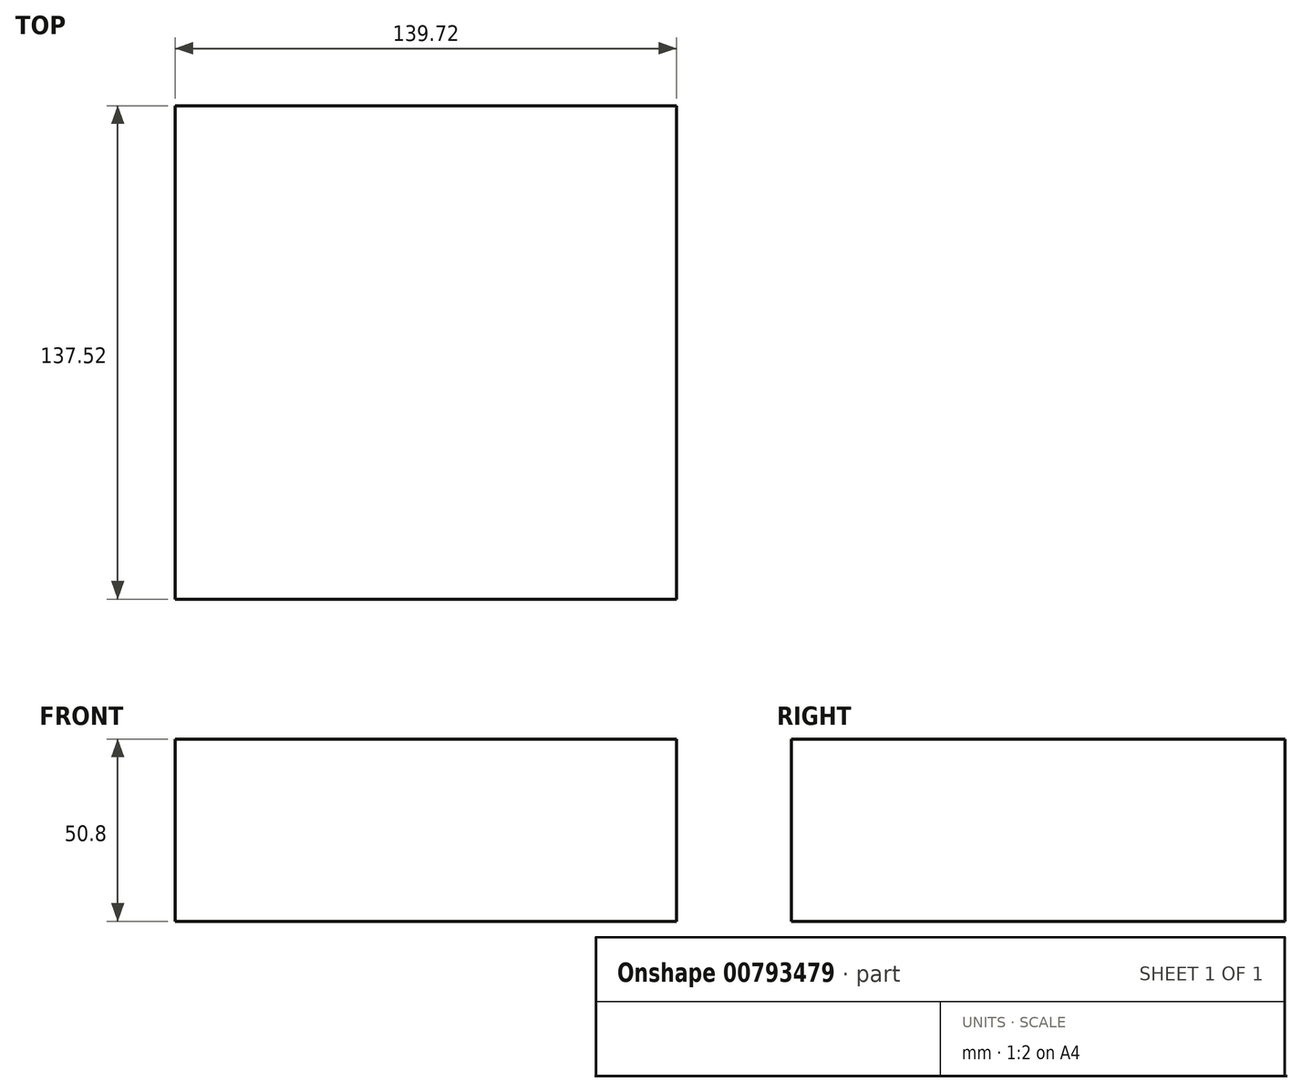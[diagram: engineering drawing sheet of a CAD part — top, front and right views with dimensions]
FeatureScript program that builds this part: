
annotation { "Feature Type Name" : "Feature", "Feature Type Description" : "" }
export const myFeature = defineFeature(function(context is Context, id is Id, definition is map)
    precondition{}
    {
        {
            var Q0;
            Q0=qCreatedBy(makeId("Top.planeOp"),FACE);
            var sketch = newSketch(context, id + "F0", { "sketchPlane" : qUnion([Q0])});
            skLineSegment(sketch, "E0.bottom", {"start": v(69.86, -68.76) * mm, "end": v(-69.86, -68.76) * mm});
            skLineSegment(sketch, "E0.top", {"start": v(69.86, 68.76) * mm, "end": v(-69.86, 68.76) * mm});
            skLineSegment(sketch, "E0.left", {"start": v(69.86, -68.76) * mm, "end": v(69.86, 68.76) * mm});
            skLineSegment(sketch, "E0.right", {"start": v(-69.86, -68.76) * mm, "end": v(-69.86, 68.76) * mm});
            skPoint(sketch, "E0.middle", {"position": v(0, 0) * mm});
            skLineSegment(sketch, "E1", {"start": v(0, 68.76) * mm, "end": v(0, -68.76) * mm});
            skSolve(sketch);
        }
        {
            var Q0;
            Q0=qCreatedBy(makeId("Top.planeOp"),FACE);
            var sketch = newSketch(context, id + "F1", { "sketchPlane" : qUnion([Q0])});
            skCircle(sketch, "E2", {"center": v(54.26, 0) * mm, "radius": 9.82 * mm});
            skSolve(sketch);
        }
        {
            var Q0;
            {var subQ0=sQuery(id+"F0.wireOp",EDGE,"E0.right");Q0=makeQuery(id+"F0.imprint","IMPRINT",FACE,{"disambiguationData":[TD([[makeQuery(id+"F0.imprint","IMPRINT",EDGE,{"derivedFrom":subQ0}),-1.0]])]});}
            var Q1;
            {var subQ0=sQuery(id+"F0.wireOp",EDGE,"E0.left");Q1=makeQuery(id+"F0.imprint","IMPRINT",FACE,{"disambiguationData":[TD([[makeQuery(id+"F0.imprint","IMPRINT",EDGE,{"derivedFrom":subQ0}),1.0]])]});}
            extrude(context, id + "F2", {"entities" : qUnion([Q0, Q1]), "depth" : -50.8 * mm, "offsetDistance" : 25.4 * mm});
        }
        {
            var Q0;
            Q0=sQuery(id+"F1.wireOp",EDGE,"E2");
            var Q1;
            Q1=sQuery(id+"F0.wireOp",EDGE,"E1");
            revolve(context, id + "F3", {"bodyType" : ToolBodyType.SURFACE, "surfaceOperationType" : NewSurfaceOperationType.NEW, "surfaceEntities" : qUnion([Q0]), "axis" : qUnion([Q1]), "revolveType" : RevolveType.FULL});
        }
    });
